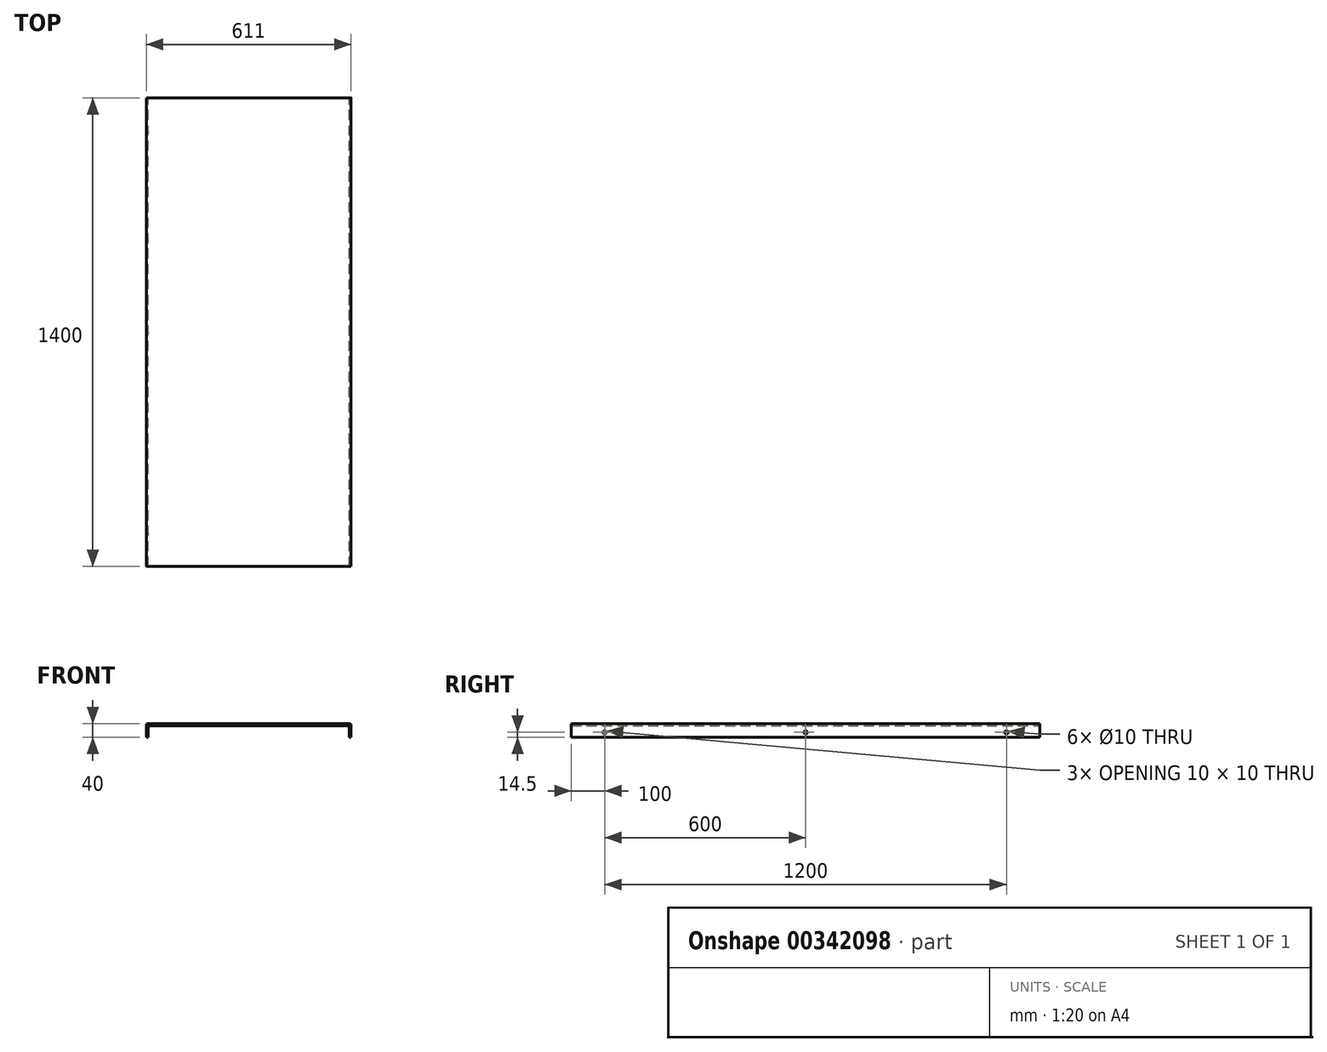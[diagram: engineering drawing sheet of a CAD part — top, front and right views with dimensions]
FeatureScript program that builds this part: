
annotation { "Feature Type Name" : "Feature", "Feature Type Description" : "" }
export const myFeature = defineFeature(function(context is Context, id is Id, definition is map)
    precondition{}
    {
        {
            var Q0;
            Q0=qCreatedBy(makeId("Front.planeOp"),FACE);
            var sketch = newSketch(context, id + "F0", { "sketchPlane" : qUnion([Q0])});
            skLineSegment(sketch, "E0", {"start": v(0, 0) * mm, "end": v(305.5, 0) * mm});
            skLineSegment(sketch, "E1", {"start": v(0, 0) * mm, "end": v(0, 40.14) * mm, "construction": true});
            skLineSegment(sketch, "E2.MirrorCS", {"start": v(0, 0) * mm, "end": v(-305.5, 0) * mm});
            skLineSegment(sketch, "E3", {"start": v(0, -5.5) * mm, "end": v(300, -5.5) * mm});
            skLineSegment(sketch, "E4", {"start": v(305.5, 0) * mm, "end": v(305.5, -40) * mm});
            skLineSegment(sketch, "E5.MirrorCS", {"start": v(-305.5, 0) * mm, "end": v(-305.5, -40) * mm});
            skLineSegment(sketch, "E6.MirrorCS", {"start": v(0, -5.5) * mm, "end": v(-300, -5.5) * mm});
            skLineSegment(sketch, "E7", {"start": v(300, -14.07) * mm, "end": v(300, -5.5) * mm});
            skLineSegment(sketch, "E8", {"start": v(300, -14.07) * mm, "end": v(300, -40) * mm});
            skLineSegment(sketch, "E9", {"start": v(305.5, -40) * mm, "end": v(300, -40) * mm});
            skLineSegment(sketch, "E10", {"start": v(-300, -5.5) * mm, "end": v(-300, -40) * mm});
            skLineSegment(sketch, "E11", {"start": v(-305.5, -40) * mm, "end": v(-300, -40) * mm});
            skSolve(sketch);
        }
        {
            var Q0;
            Q0=qSketchRegion(id+"F0",true);
            extrude(context, id + "F1", {"entities" : qUnion([Q0]), "depth" : 1400 * mm});
        }
        {
            var Q0;
            Q0=makeQuery(id+"F1.opExtrude","SWEPT_FACE",FACE,{"disambiguationData":[OSD([sQuery(id+"F0.wireOp",EDGE,"E5.MirrorCS")])]});
            var sketch = newSketch(context, id + "F2", { "sketchPlane" : qUnion([Q0])});
            skCircle(sketch, "E12", {"center": v(100, -20) * mm, "radius": 5 * mm});
            skPoint(sketch, "E12.centerSnap0", {"position": v(0, -20) * mm});
            skCircle(sketch, "E13", {"center": v(1300, -20) * mm, "radius": 5 * mm});
            skPoint(sketch, "E13.centerSnap0", {"position": v(1400, -20) * mm});
            skLineSegment(sketch, "E14", {"start": v(99.77, 0) * mm, "end": v(99.77, -5.5) * mm});
            skLineSegment(sketch, "E15", {"start": v(99.77, -5.5) * mm, "end": v(1400, -5.5) * mm});
            skLineSegment(sketch, "E16.0", {"start": v(1400, 0) * mm, "end": v(1400, -40) * mm});
            skLineSegment(sketch, "E17", {"start": v(99.77, -5.5) * mm, "end": v(0, -5.5) * mm});
            skLineSegment(sketch, "E18.0", {"start": v(0, 0) * mm, "end": v(0, -40) * mm});
            skLineSegment(sketch, "E19", {"start": v(100, -20) * mm, "end": v(100, -25.5) * mm});
            skLineSegment(sketch, "E20", {"start": v(900, -20) * mm, "end": v(900, -25.5) * mm});
            skLineSegment(sketch, "E21", {"start": v(1300, -20) * mm, "end": v(1300, -25.5) * mm});
            skLineSegment(sketch, "E22", {"start": v(100, -25.5) * mm, "end": v(700, -25.5) * mm});
            skLineSegment(sketch, "E23", {"start": v(700, -25.5) * mm, "end": v(1300, -25.5) * mm});
            skSolve(sketch);
        }
        {
            var Q0;
            Q0=makeQuery(id+"F1.opExtrude","SWEPT_EDGE",EDGE,{"disambiguationData":[OSD([sQuery(id+"F0.wireOp",EDGE,"E2.MirrorCS"),sQuery(id+"F0.wireOp",EDGE,"E5.MirrorCS")])]});
            var Q1;
            Q1=makeQuery(id+"F1.opExtrude","SWEPT_EDGE",EDGE,{"disambiguationData":[OSD([sQuery(id+"F0.wireOp",EDGE,"E0"),sQuery(id+"F0.wireOp",EDGE,"E4")])]});
            fillet(context, id + "F3", {"entities" : qUnion([Q0, Q1]), "radius" : 3 * mm, "tangentPropagation" : true, "allowEdgeOverflow" : false});
        }
        {
            var Q0;
            Q0=sQuery(id+"F2.wireOp",VERTEX,"E19.end");
            var Q1;
            Q1=sQuery(id+"F2.wireOp",VERTEX,"E22.end");
            var Q2;
            Q2=sQuery(id+"F2.wireOp",VERTEX,"E21.end");
            var Q3;
            Q3=makeQuery(id+"F1.opExtrude","SWEPT_BODY",BODY,{"disambiguationData":[OSD([sQuery(id+"F0.wireOp",EDGE,"E0"),sQuery(id+"F0.wireOp",EDGE,"E2.MirrorCS"),sQuery(id+"F0.wireOp",EDGE,"E3"),sQuery(id+"F0.wireOp",EDGE,"E4"),sQuery(id+"F0.wireOp",EDGE,"E5.MirrorCS"),sQuery(id+"F0.wireOp",EDGE,"E6.MirrorCS"),sQuery(id+"F0.wireOp",EDGE,"E7"),sQuery(id+"F0.wireOp",EDGE,"E8"),sQuery(id+"F0.wireOp",EDGE,"E9"),sQuery(id+"F0.wireOp",EDGE,"E10"),sQuery(id+"F0.wireOp",EDGE,"E11")])]});
            hole(context, id + "F4", {"style" : HoleStyle.SIMPLE, "endStyle" : HoleEndStyle.BLIND, "holeDiameter" : 10 * mm, "holeDepth" : 3000 * mm, "tappedDepth" : 12 * mm, "tapClearance" : 3, "locations" : qUnion([Q0, Q1, Q2]), "scope" : qUnion([Q3])});
        }
    });
